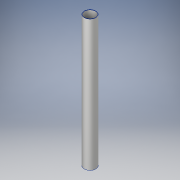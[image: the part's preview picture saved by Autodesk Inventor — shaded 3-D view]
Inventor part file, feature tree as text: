
AUTODESK INVENTOR PART (.ipt)
format: ipt  version: 2017 (Build 210142000, 142)  size: 94,208 bytes
history: native  units: in
note: dims shown in document units (in); Inventor stores cm internally (conversion verified against a paired STEP export)
features: extrude x1, sketch x1
ambient origin geometry x8: Origin, YZ Plane, XZ Plane, XY Plane, X Axis, Y Axis, Z Axis, Center Point
bodies: Solid1 (feature_tree)
feature tree (2):
  extrude  "Extrusion1"  Depth=90.0in
  sketch  "Sketch1"  dims[d0=8.0in d1=7.5in d2=90.0in d3=0.0in]
